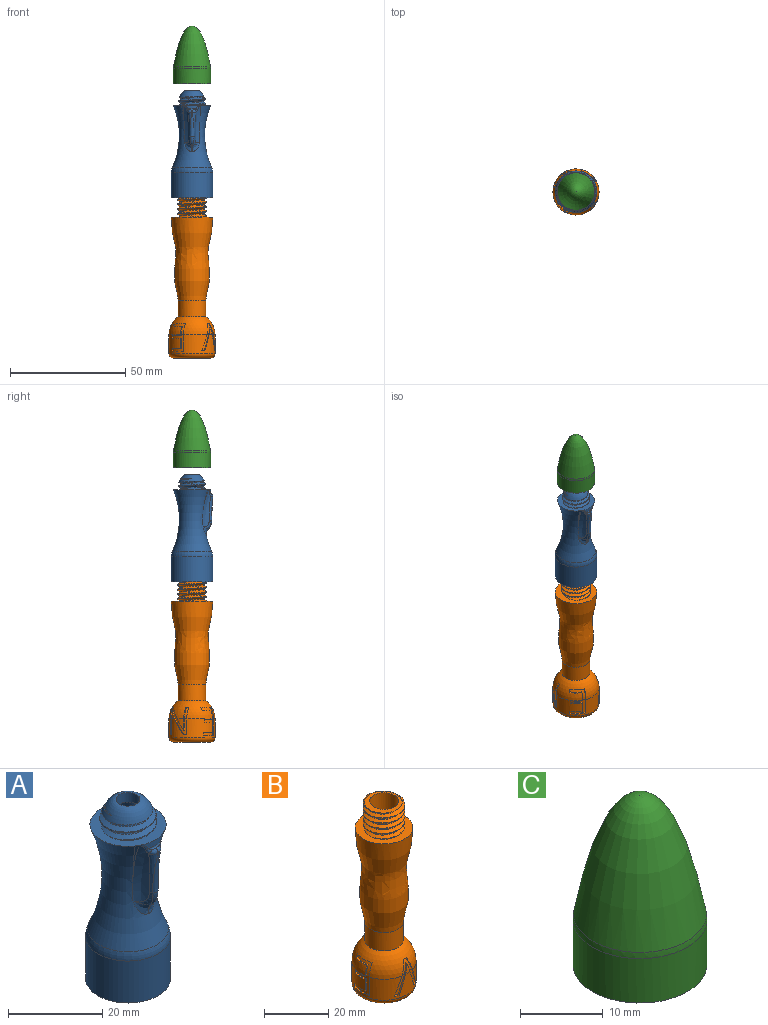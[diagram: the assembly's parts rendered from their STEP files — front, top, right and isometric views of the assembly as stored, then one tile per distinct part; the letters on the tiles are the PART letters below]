
ASSEMBLY  parts=3 mates=2
PART A: 50 faces, bbox 33.8x33.8x52.5 mm
  f0: cylinder r=6mm len=12mm, axis (0,0,-1), area 11.8mm2, adj f1,f26,f27,f49
  f1: plane 16.74x16.74mm, normal (0,0,1), area 114.4mm2, adj f0,f25,f26,f27,f29,f30,f35,f37
  f2: bspline ~20.46x7.27mm, area 45.8mm2, adj f5,f29,f32,f41,f42
  f3: bspline ~20.46x7.27mm, area 45.8mm2, adj f4,f29,f30,f31,f37,f38
  f4: bspline ~14.25x2.72mm, area 12.3mm2, adj f3,f31,f39,f44
  f5: bspline ~14.03x2.72mm, area 12.3mm2, adj f2,f32,f40,f44
  f6: plane 18.59x18.59mm, normal (0,0,-1), area 118.9mm2, adj f7,f13,f14,f15,f23
  f7: cylinder r=9mm len=18mm, axis (0,0,-1), area 615mm2, adj f6,f47
  f8: cone r=4mm half-angle=20.6deg, axis (0,0,-1), area 87.2mm2, adj f9,f48
  f9: cylinder r=4mm len=25.01mm, axis (0,0,-1), area 628.6mm2, adj f8,f28
  f10: bspline ~13.88x13.44mm, area 27.2mm2, adj f12,f14,f16,f17,f24
  f11: bspline ~13.88x13.44mm, area 27.2mm2, adj f12,f13,f16,f24
  f12: bspline ~14.06x13.62mm, area 12.2mm2, adj f10,f11,f15,f24
  f13: bspline ~16.53x14.32mm, area 303.9mm2, adj f6,f11,f15,f17,f18,f19,f20,f21
  f14: bspline ~16.53x14.32mm, area 281.4mm2, adj f6,f10,f15,f18,f19,f20,f21,f22
  f15: bspline ~16.74x14.5mm, area 73.8mm2, adj f6,f12,f13,f14
  f16: cylinder r=6.08mm len=12.15mm, axis (0,0,-1), area 49.2mm2, adj f10,f11,f17,f24,f28
  f17: cylinder r=6.08mm len=12.15mm, axis (0,0,-1), area 30.1mm2, adj f10,f13,f16,f18
  f18: cylinder r=6.08mm len=12.15mm, axis (0,0,-1), area 19.1mm2, adj f13,f14,f17,f19
  f19: cylinder r=6.08mm len=12.15mm, axis (0,0,-1), area 19.1mm2, adj f13,f14,f18,f20
  f20: cylinder r=6.08mm len=12.15mm, axis (0,0,-1), area 19.1mm2, adj f13,f14,f19,f21
  f21: cylinder r=6.08mm len=12.15mm, axis (0,0,-1), area 19.1mm2, adj f13,f14,f20,f22
  f22: cylinder r=6.08mm len=12.15mm, axis (0,0,-1), area 19.1mm2, adj f13,f14,f21,f23
  f23: cylinder r=6.08mm len=6.08mm, axis (0,0,-1), area 2.4mm2, adj f6,f14,f22
  f24: plane 0.35x0.15mm, normal (0,1,-0.01), area 0mm2, adj f10,f11,f12,f16
  f25: bspline ~11.36x9.84mm, area 39.2mm2, adj f1,f26,f27,f49
  f26: bspline ~13.86x12mm, area 76.5mm2, adj f0,f1,f25,f49
  f27: bspline ~13.86x12mm, area 75.2mm2, adj f0,f1,f25,f49
  f28: cone r=6.08mm half-angle=64.5deg, axis (0,0,-1), area 72.8mm2, adj f9,f16
  f29: torus R=39.39mm, axis (0,0,-1), area 988.5mm2, adj f1,f2,f3,f30,f33,f34,f42,f47
  f30: torus R=39.39mm, axis (0,0,-1), area 3.4mm2, adj f1,f3,f29,f37
  f31: bspline ~7.36x5.96mm, area 6.3mm2, adj f3,f4,f34,f45
  f32: bspline ~7.25x5.59mm, area 6.3mm2, adj f2,f5,f33,f45
  f33: bspline ~4.22x3.64mm, area 5.3mm2, adj f29,f32,f46
  f34: bspline ~4.22x3.64mm, area 5.4mm2, adj f29,f31,f46
  f35: cylinder r=8.09mm len=6.25mm, axis (0,0,1), area 7.6mm2, adj f1,f36,f37,f42
  f36: torus R=8.59mm, axis (0,0,1), area 1.3mm2, adj f35,f38,f39,f40,f41
  f37: bspline ~3.27x2.56mm, area 1.5mm2, adj f1,f3,f30,f35,f38
  f38: bspline ~1.72x1.55mm, area 1mm2, adj f3,f36,f37,f39
  f39: bspline ~1.93x1.11mm, area 1.9mm2, adj f4,f36,f38,f43
  f40: bspline ~2.08x1.45mm, area 1.9mm2, adj f5,f36,f41,f43
  f41: bspline ~1.51x1.4mm, area 1mm2, adj f2,f36,f40,f42
  f42: bspline ~3.27x2.56mm, area 1.5mm2, adj f1,f2,f29,f35,f41
  f43: sphere r=1mm, area 0.1mm2, adj f39,f40,f44
  f44: bspline ~12.61x1.63mm, area 13.9mm2, adj f4,f5,f43,f45
  f45: bspline ~4.33x2.46mm, area 6mm2, adj f31,f32,f44,f46
  f46: bspline ~3.09x1.16mm, area 0.6mm2, adj f33,f34,f45
  f47: torus R=4mm, axis (0,0,1), area 118.8mm2, adj f7,f29
  f48: cylinder r=2.5mm len=5mm, axis (0,0,1), area 39.3mm2, adj f8,f49
  f49: revolved ~12x12mm, area 112mm2, adj f0,f25,f26,f27,f48
PART B: 94 faces, bbox 22.2x22.2x72.3 mm
  f0: sphere r=10mm, area 3.4mm2, adj f2,f83,f87,f90,f91
  f1: sphere r=10mm, area 430.4mm2, adj f2,f3,f6,f16,f35,f36,f37,f38
  f2: cylinder r=10mm len=20mm, axis (0,0,1), area 394.5mm2, adj f0,f1,f3,f4,f5,f19,f20,f21
  f3: cylinder r=10mm len=0.72mm, axis (0,0,1), area 0.1mm2, adj f1,f2,f19
  f4: cylinder r=10mm len=4.12mm, axis (0,0,1), area 6.9mm2, adj f2,f22,f23,f24,f25,f26
  f5: sphere r=10mm, area 3.2mm2, adj f2,f56,f62,f63,f64
  f6: cylinder r=10mm len=4.98mm, axis (0,0,1), area 8.1mm2, adj f1,f53,f57,f58,f59
  f7: plane 18.56x18.56mm, normal (0,0,1), area 145.5mm2, adj f9,f11,f12,f13,f15
  f8: cylinder r=4.5mm len=43mm, axis (0,0,-1), area 1215.8mm2, adj f10,f14
  f9: cylinder r=6.5mm len=13mm, axis (0,0,-1), area 52mm2, adj f7,f10,f12,f13
  f10: plane 12.39x12.32mm, normal (0,0,1), area 45.3mm2, adj f8,f9,f11,f12,f13
  f11: bspline ~12.51x11.5mm, area 94.1mm2, adj f7,f10,f12,f13
  f12: bspline ~15.01x13mm, area 234.2mm2, adj f7,f9,f10,f11
  f13: bspline ~15.01x13mm, area 234.4mm2, adj f7,f9,f10,f11
  f14: plane 9x9mm, normal (0,0,1), area 63.6mm2, adj f8
  f15: revolved ~36x18mm, area 1724.2mm2, adj f7,f16
  f16: cylinder r=6mm len=12mm, axis (0,0,1), area 263.9mm2, adj f1,f15
  f17: plane 16x16mm, normal (0,0,-1), area 201.1mm2, adj f93
  f18: cylinder r=9.5mm len=7.07mm, axis (0,0,1), area 19.7mm2, adj f19,f20,f21,f22,f23,f24,f25,f26
  f19: extruded ~1.34x0.53mm, area 0.7mm2, adj f2,f3,f18,f33,f38
  f20: extruded ~0.57x0.15mm, area 0.1mm2, adj f2,f18,f21,f37
  f21: extruded ~2.58x1.43mm, area 1.5mm2, adj f2,f18,f20,f22
  f22: extruded ~1.66x0.73mm, area 0.9mm2, adj f2,f4,f18,f21,f23
  f23: extruded ~0.77x0.73mm, area 0.5mm2, adj f4,f18,f22,f24
  f24: extruded ~1.01x0.57mm, area 0.5mm2, adj f4,f18,f23,f25
  f25: extruded ~1.31x0.64mm, area 0.8mm2, adj f4,f18,f24,f26
  f26: extruded ~1.72x0.65mm, area 0.9mm2, adj f2,f4,f18,f25,f27
  f27: extruded ~2.86x0.95mm, area 1.5mm2, adj f2,f18,f26,f28
  f28: plane 1.21x0.68mm, normal (0,0.94,-0.34), area 0.7mm2, adj f2,f18,f27,f29
  f29: extruded ~3.26x1.1mm, area 1.7mm2, adj f2,f18,f28,f30
  f30: extruded ~2.74x0.88mm, area 1.5mm2, adj f2,f18,f29,f31
  f31: extruded ~2.19x1.03mm, area 1.3mm2, adj f2,f18,f30,f32
  f32: extruded ~2.12x0.79mm, area 1.2mm2, adj f2,f18,f31,f33
  f33: extruded ~2.37x1.41mm, area 1.4mm2, adj f2,f18,f19,f32
  f34: sphere r=9.5mm, area 15mm2, adj f18,f35,f36,f37,f38,f39,f40,f41
  f35: extruded ~3.09x0.88mm, area 1.9mm2, adj f1,f34,f36,f46
  f36: extruded ~2.45x1.14mm, area 1.6mm2, adj f1,f34,f35,f37
  f37: extruded ~1.83x0.94mm, area 1.1mm2, adj f1,f20,f34,f36
  f38: extruded ~0.55x0.43mm, area 0.2mm2, adj f1,f19,f34,f39
  f39: extruded ~0.83x0.73mm, area 0.6mm2, adj f1,f34,f38,f40
  f40: extruded ~1.01x0.73mm, area 0.5mm2, adj f1,f34,f39,f41
  f41: extruded ~1.46x0.82mm, area 0.9mm2, adj f1,f34,f40,f42
  f42: extruded ~2.08x0.65mm, area 1.2mm2, adj f1,f34,f41,f43
  f43: extruded ~1.71x0.75mm, area 1mm2, adj f1,f34,f42,f44
  f44: extruded ~1.6x0.94mm, area 1mm2, adj f1,f34,f43,f45
  f45: plane 1.37x1.31mm, normal (0,-1,0), area 0.8mm2, adj f1,f34,f44,f46
  f46: extruded ~3.26x1.19mm, area 2mm2, adj f1,f34,f35,f45
  f47: cylinder r=9.5mm len=6.9mm, axis (0,0,1), area 10mm2, adj f48,f49,f50,f51,f60
  f48: extruded ~0.54x0.07mm, area 0mm2, adj f2,f47,f49,f64
  f49: plane 6.83x0.54mm, normal (1,0,0), area 3.7mm2, adj f2,f47,f48,f50
  f50: plane 1.29x1.19mm, normal (0,0,1), area 0.7mm2, adj f2,f47,f49,f51
  f51: plane 12.37x2.78mm, normal (-1,0,0), area 7.1mm2, adj f1,f2,f47,f50,f60,f61
  f52: cylinder r=9.5mm len=6.9mm, axis (0,0,1), area 19.2mm2, adj f53,f54,f55,f56,f57,f58,f59,f60
  f53: extruded ~3.22x0.57mm, area 1.7mm2, adj f6,f52,f57,f58
  f54: plane 12.37x2.67mm, normal (1,0,0), area 6.8mm2, adj f1,f2,f52,f55,f65,f66
  f55: plane 1.56x1.16mm, normal (0,0,1), area 0.8mm2, adj f2,f52,f54,f56
  f56: plane 10.01x6.55mm, normal (-0.84,0,0.55), area 6.1mm2, adj f2,f5,f52,f55,f60,f62
  f57: plane 0.55x0.07mm, normal (0,0,-1), area 0mm2, adj f6,f52,f53,f59
  f58: plane 7.07x2.36mm, normal (-1,0,0), area 3.7mm2, adj f1,f6,f52,f53,f65,f66
  f59: plane 10.29x6.8mm, normal (0.84,0,-0.55), area 6.2mm2, adj f1,f6,f52,f57,f60,f61
  f60: sphere r=9.5mm, area 14.8mm2, adj f47,f51,f52,f56,f59,f61,f62,f63
  f61: plane 1.58x1.58mm, normal (0,0,-1), area 1.1mm2, adj f1,f51,f59,f60
  f62: plane 0.6x0.07mm, normal (0,0,1), area 0mm2, adj f5,f56,f60,f63
  f63: extruded ~1.41x0.97mm, area 0.8mm2, adj f5,f60,f62,f64
  f64: extruded ~1.64x0.71mm, area 0.9mm2, adj f5,f48,f60,f63
  f65: sphere r=9.5mm, area 7.7mm2, adj f52,f54,f58,f66
  f66: plane 1.3x1.28mm, normal (0,0,-1), area 0.8mm2, adj f1,f54,f58,f65
  f67: cylinder r=9.5mm len=7mm, axis (0,0,1), area 22.7mm2, adj f68,f69,f70,f71,f72,f73,f74,f75
  f68: plane 6.63x1.21mm, normal (0,0,1), area 3.4mm2, adj f2,f67,f69,f76
  f69: plane 1.24x0.54mm, normal (0,-1,0), area 0.7mm2, adj f2,f67,f68,f70
  f70: plane 5.25x1.21mm, normal (0,0,-1), area 2.7mm2, adj f2,f67,f69,f71
  f71: plane 4.38x0.51mm, normal (0,-1,0), area 2.2mm2, adj f2,f67,f70,f72
  f72: plane 4.93x1.08mm, normal (0,0,1), area 2.5mm2, adj f2,f67,f71,f73
  f73: plane 1.22x0.53mm, normal (0,-1,0), area 0.6mm2, adj f2,f67,f72,f74
  f74: plane 4.93x1.08mm, normal (0,0,-1), area 2.5mm2, adj f2,f67,f73,f75
  f75: plane 3.91x1.33mm, normal (0,-1,0), area 2mm2, adj f1,f2,f67,f74,f77,f79
  f76: plane 12.18x2.26mm, normal (0,1,0), area 6.4mm2, adj f1,f2,f67,f68,f77,f78
  f77: sphere r=9.5mm, area 15.2mm2, adj f67,f75,f76,f78,f79,f80
  f78: plane 6.63x1.41mm, normal (0,0,-1), area 3.9mm2, adj f1,f76,f77,f80
  f79: plane 5.25x1.31mm, normal (0,0,1), area 2.9mm2, adj f1,f75,f77,f80
  f80: plane 1.31x1.26mm, normal (0,-1,0), area 0.8mm2, adj f1,f77,f78,f79
  f81: cylinder r=9.5mm len=6.9mm, axis (0,0,1), area 10.6mm2, adj f82,f83,f84,f89
  f82: plane 1.49x1.15mm, normal (0,0,1), area 0.8mm2, adj f2,f81,f83,f84
  f83: plane 7.74x2.8mm, normal (-0.94,0,0.33), area 4.1mm2, adj f0,f2,f81,f82,f89,f90
  f84: plane 12.07x4.46mm, normal (0.94,0,-0.34), area 6.7mm2, adj f1,f2,f81,f82,f89,f92
  f85: cylinder r=9.5mm len=6.9mm, axis (0,0,1), area 11mm2, adj f86,f87,f88,f89
  f86: plane 12.16x4.52mm, normal (-0.94,0,-0.34), area 7mm2, adj f1,f2,f85,f88,f89,f92
  f87: plane 7.84x2.88mm, normal (0.94,0,0.33), area 4.3mm2, adj f0,f2,f85,f88,f89,f91
  f88: plane 1.47x1.4mm, normal (0,0,1), area 0.8mm2, adj f2,f85,f86,f87
  f89: sphere r=9.5mm, area 13.4mm2, adj f81,f83,f84,f85,f86,f87,f90,f91
  f90: extruded ~2.63x1.11mm, area 1.4mm2, adj f0,f83,f89,f91
  f91: extruded ~2.58x1.02mm, area 1.4mm2, adj f0,f87,f89,f90
  f92: plane 1.37x0.68mm, normal (0,0,-1), area 0.8mm2, adj f1,f84,f86,f89
  f93: torus R=8mm, axis (0,0,1), area 183mm2, adj f2,f17
PART C: 11 faces, bbox 16.8x16.8x16.4 mm
  f0: plane 16.77x16.77mm, normal (0,0,-1), area 92.9mm2, adj f1,f5,f6,f7,f9
  f1: cylinder r=8.09mm len=16.18mm, axis (0,0,-1), area 334mm2, adj f0,f10
  f2: revolved ~0x0mm, area 0mm2, adj f10
  f3: cone r=6.5mm half-angle=39.1deg, axis (0,0,-1), area 210.5mm2, adj f4,f8
  f4: plane 4.91x4.82mm, normal (0,0,-1), area 0.7mm2, adj f3,f5,f6,f7
  f5: bspline ~15.2x13.17mm, area 166.3mm2, adj f0,f4,f7,f8,f9
  f6: bspline ~15.2x13.17mm, area 166.2mm2, adj f0,f4,f7,f8,f9
  f7: bspline ~15.41x13.35mm, area 42.2mm2, adj f0,f4,f5,f6
  f8: plane 13.49x13.49mm, normal (0,0,1), area 20.6mm2, adj f3,f5,f6,f9
  f9: cylinder r=5.5mm len=11mm, axis (0,0,1), area 61.6mm2, adj f0,f5,f6,f8
  f10: torus R=3.09mm, axis (0,0,1), area 43.9mm2, adj f1,f2
PLACE A t=(-27.06,-1.94,-42.01)mm fixed
PLACE B rot(axis=(0,0,1),50.9deg) t=(-27.06,-1.94,-83.51)mm
PLACE C rot(axis=(0,0,-1),10.6deg) t=(-27.06,-1.94,7.49)mm
MATE cylindrical C.f3 <-> A.f48  axis (0,0,-1) through (-27.06,-1.94,14.49)mm
MATE cylindrical B.f8 <-> A.f7  axis (0,0,-1) through (-27.06,-1.94,-62.01)mm
